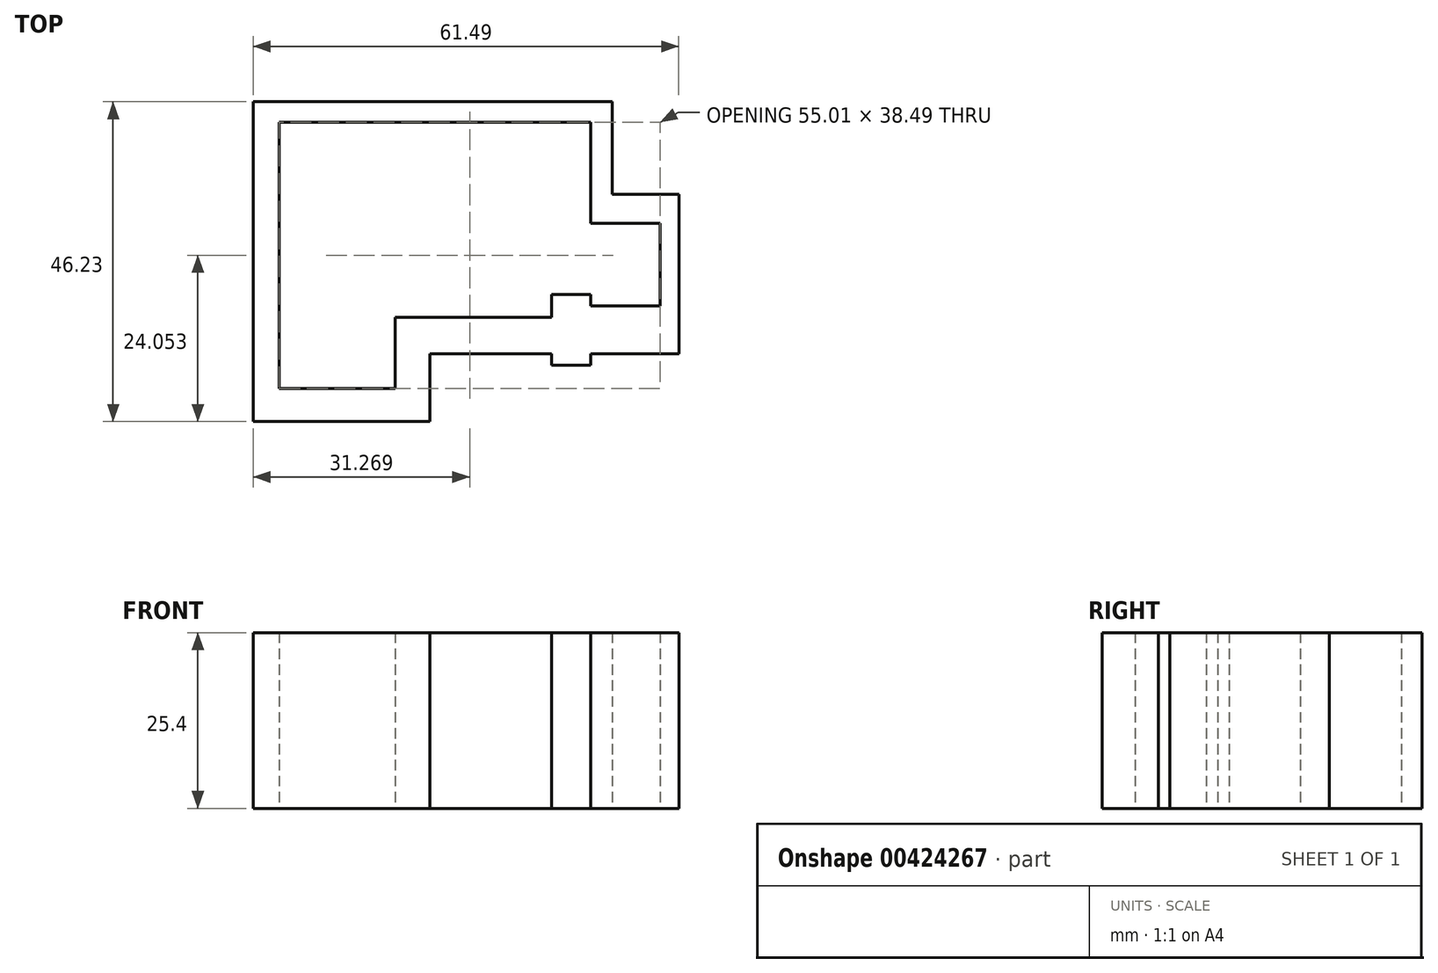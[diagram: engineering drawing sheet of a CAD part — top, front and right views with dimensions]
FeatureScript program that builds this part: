
annotation { "Feature Type Name" : "Feature", "Feature Type Description" : "" }
export const myFeature = defineFeature(function(context is Context, id is Id, definition is map)
    precondition{}
    {
        {
            var Q0;
            Q0=qCreatedBy(makeId("Top.planeOp"),FACE);
            var sketch = newSketch(context, id + "F0", { "sketchPlane" : qUnion([Q0])});
            skLineSegment(sketch, "E0.bottom", {"start": v(5.86, 65.37) * mm, "end": v(9.62, 65.37) * mm});
            skLineSegment(sketch, "E0.top", {"start": v(5.86, 44.03) * mm, "end": v(9.62, 44.03) * mm});
            skLineSegment(sketch, "E0.left", {"start": v(5.86, 65.37) * mm, "end": v(5.86, 44.03) * mm});
            skLineSegment(sketch, "E0.right", {"start": v(9.62, 65.37) * mm, "end": v(9.62, 44.03) * mm});
            skLineSegment(sketch, "E1.top", {"start": v(5.86, 22.07) * mm, "end": v(9.62, 22.07) * mm});
            skLineSegment(sketch, "E1.left", {"start": v(5.86, 44.03) * mm, "end": v(5.86, 22.07) * mm});
            skLineSegment(sketch, "E1.right", {"start": v(9.62, 44.03) * mm, "end": v(9.62, 22.07) * mm});
            skLineSegment(sketch, "E2.bottom", {"start": v(11.5, 22.07) * mm, "end": v(9.62, 22.07) * mm});
            skLineSegment(sketch, "E2.top", {"start": v(11.5, 26.88) * mm, "end": v(9.62, 26.88) * mm});
            skLineSegment(sketch, "E2.left", {"start": v(11.5, 22.07) * mm, "end": v(11.5, 26.88) * mm});
            skLineSegment(sketch, "E2.right", {"start": v(9.62, 22.07) * mm, "end": v(9.62, 26.88) * mm});
            skLineSegment(sketch, "E3.bottom", {"start": v(11.5, 26.88) * mm, "end": v(31.38, 26.88) * mm});
            skLineSegment(sketch, "E3.top", {"start": v(11.5, 22.07) * mm, "end": v(31.38, 22.07) * mm});
            skLineSegment(sketch, "E3.left", {"start": v(11.5, 26.88) * mm, "end": v(11.5, 22.07) * mm});
            skLineSegment(sketch, "E3.right", {"start": v(31.38, 26.88) * mm, "end": v(31.38, 22.07) * mm});
            skLineSegment(sketch, "E4.bottom", {"start": v(31.38, 26.88) * mm, "end": v(26.36, 26.88) * mm});
            skLineSegment(sketch, "E4.top", {"start": v(31.38, 37.13) * mm, "end": v(26.36, 37.13) * mm});
            skLineSegment(sketch, "E4.left", {"start": v(31.38, 26.88) * mm, "end": v(31.38, 37.13) * mm});
            skLineSegment(sketch, "E4.right", {"start": v(26.36, 26.88) * mm, "end": v(26.36, 37.13) * mm});
            skLineSegment(sketch, "E5.bottom", {"start": v(31.38, 37.13) * mm, "end": v(51.46, 37.13) * mm});
            skLineSegment(sketch, "E5.top", {"start": v(31.38, 31.9) * mm, "end": v(51.46, 31.9) * mm});
            skLineSegment(sketch, "E5.left", {"start": v(31.38, 37.13) * mm, "end": v(31.38, 31.9) * mm});
            skLineSegment(sketch, "E5.right", {"start": v(51.46, 37.13) * mm, "end": v(51.46, 31.9) * mm});
            skLineSegment(sketch, "E6.bottom", {"start": v(48.95, 30.23) * mm, "end": v(54.6, 30.23) * mm});
            skLineSegment(sketch, "E6.top", {"start": v(48.95, 40.48) * mm, "end": v(54.6, 40.48) * mm});
            skLineSegment(sketch, "E6.left", {"start": v(48.95, 30.23) * mm, "end": v(48.95, 40.48) * mm});
            skLineSegment(sketch, "E6.right", {"start": v(54.6, 30.23) * mm, "end": v(54.6, 40.48) * mm});
            skLineSegment(sketch, "E7.bottom", {"start": v(54.6, 38.8) * mm, "end": v(67.35, 38.8) * mm});
            skLineSegment(sketch, "E7.top", {"start": v(54.6, 31.9) * mm, "end": v(67.35, 31.9) * mm});
            skLineSegment(sketch, "E7.left", {"start": v(54.6, 38.8) * mm, "end": v(54.6, 31.9) * mm});
            skLineSegment(sketch, "E7.right", {"start": v(67.35, 38.8) * mm, "end": v(67.35, 31.9) * mm});
            skLineSegment(sketch, "E8.bottom", {"start": v(64.64, 38.8) * mm, "end": v(67.35, 38.8) * mm});
            skLineSegment(sketch, "E8.top", {"start": v(64.64, 54.9) * mm, "end": v(67.35, 54.9) * mm});
            skLineSegment(sketch, "E8.left", {"start": v(64.64, 38.8) * mm, "end": v(64.64, 54.9) * mm});
            skLineSegment(sketch, "E8.right", {"start": v(67.35, 38.8) * mm, "end": v(67.35, 54.9) * mm});
            skLineSegment(sketch, "E9.bottom", {"start": v(64.64, 54.9) * mm, "end": v(54.6, 54.9) * mm});
            skLineSegment(sketch, "E9.top", {"start": v(64.64, 50.73) * mm, "end": v(54.6, 50.73) * mm});
            skLineSegment(sketch, "E9.left", {"start": v(64.64, 54.9) * mm, "end": v(64.64, 50.73) * mm});
            skLineSegment(sketch, "E9.right", {"start": v(54.6, 54.9) * mm, "end": v(54.6, 50.73) * mm});
            skLineSegment(sketch, "E10.bottom", {"start": v(54.6, 54.9) * mm, "end": v(57.73, 54.9) * mm});
            skLineSegment(sketch, "E10.top", {"start": v(54.6, 68.3) * mm, "end": v(57.73, 68.3) * mm});
            skLineSegment(sketch, "E10.left", {"start": v(54.6, 54.9) * mm, "end": v(54.6, 68.3) * mm});
            skLineSegment(sketch, "E10.right", {"start": v(57.73, 54.9) * mm, "end": v(57.73, 68.3) * mm});
            skLineSegment(sketch, "E11.bottom", {"start": v(54.6, 68.3) * mm, "end": v(5.86, 68.3) * mm});
            skLineSegment(sketch, "E11.top", {"start": v(54.6, 65.37) * mm, "end": v(5.86, 65.37) * mm});
            skLineSegment(sketch, "E11.left", {"start": v(54.6, 68.3) * mm, "end": v(54.6, 65.37) * mm});
            skLineSegment(sketch, "E11.right", {"start": v(5.86, 68.3) * mm, "end": v(5.86, 65.37) * mm});
            skSolve(sketch);
        }
        {
            var Q0;
            Q0 = qSketchRegion(id + "F0", true);
            extrude(context, id + "F1", {"entities" : qUnion([Q0]), "depth" : 25.4 * mm});
        }
    });
